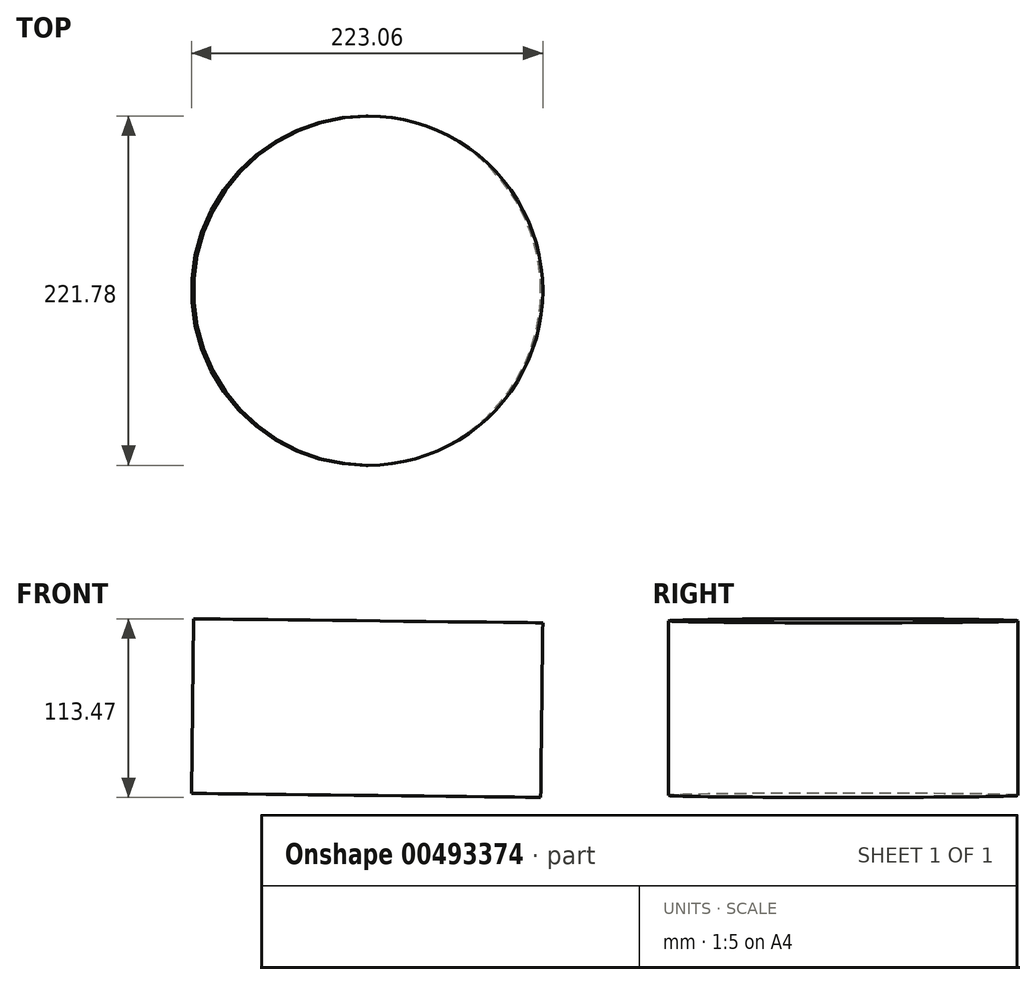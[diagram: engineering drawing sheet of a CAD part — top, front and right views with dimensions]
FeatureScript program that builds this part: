
annotation { "Feature Type Name" : "Feature", "Feature Type Description" : "" }
export const myFeature = defineFeature(function(context is Context, id is Id, definition is map)
    precondition{}
    {
        {
            var Q0;
            Q0=qCreatedBy(makeId("Front.planeOp"),FACE);
            var sketch = newSketch(context, id + "F0", { "sketchPlane" : qUnion([Q0])});
            skCircle(sketch, "E0.cCircle", {"center": v(0, 0) * mm, "radius": 78.41 * mm, "construction": true});
            skLineSegment(sketch, "E0.0", {"start": v(-54.8, 56.09) * mm, "end": v(56.09, 54.8) * mm});
            skLineSegment(sketch, "E0.1", {"start": v(56.09, 54.8) * mm, "end": v(54.8, -56.09) * mm});
            skLineSegment(sketch, "E0.2", {"start": v(54.8, -56.09) * mm, "end": v(-56.09, -54.8) * mm});
            skLineSegment(sketch, "E0.3", {"start": v(-56.09, -54.8) * mm, "end": v(-54.8, 56.09) * mm});
            skSolve(sketch);
        }
        {
            var Q0;
            Q0=makeQuery(id+"F0.imprint","IMPRINT",FACE,{"disambiguationData":[TD([[makeQuery(id+"F0.imprint","IMPRINT",EDGE,{"derivedFrom":sQuery(id+"F0.wireOp",EDGE,"E0.0")}),-1.0]])]});
            var Q1;
            Q1=sQuery(id+"F0.wireOp",EDGE,"E0.1");
            revolve(context, id + "F1", {"entities" : qUnion([Q0]), "axis" : qUnion([Q1]), "revolveType" : RevolveType.FULL});
        }
    });
